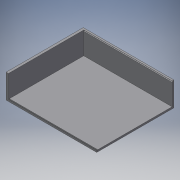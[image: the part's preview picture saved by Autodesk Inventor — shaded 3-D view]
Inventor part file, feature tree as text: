
AUTODESK INVENTOR PART (.ipt)
format: ipt  version: 2016 SP2 (Build 200236200, 236)  size: 102,400 bytes
history: native  units: mm
features: other x3, sketch x2
ambient origin geometry x8: Origin, YZ Plane, XZ Plane, XY Plane, X Axis, Y Axis, Z Axis, Center Point
bodies: Volumenkörper1 (feature_tree)
feature tree (5):
  other  "Batcap2.ipt"
  other  "Volumenkörper1::Batcap2.ipt"
  other  "Bezeichnung1"
  sketch  "Skizze1"  dims[d0=10.0mm]
  sketch  "Skizze2"
